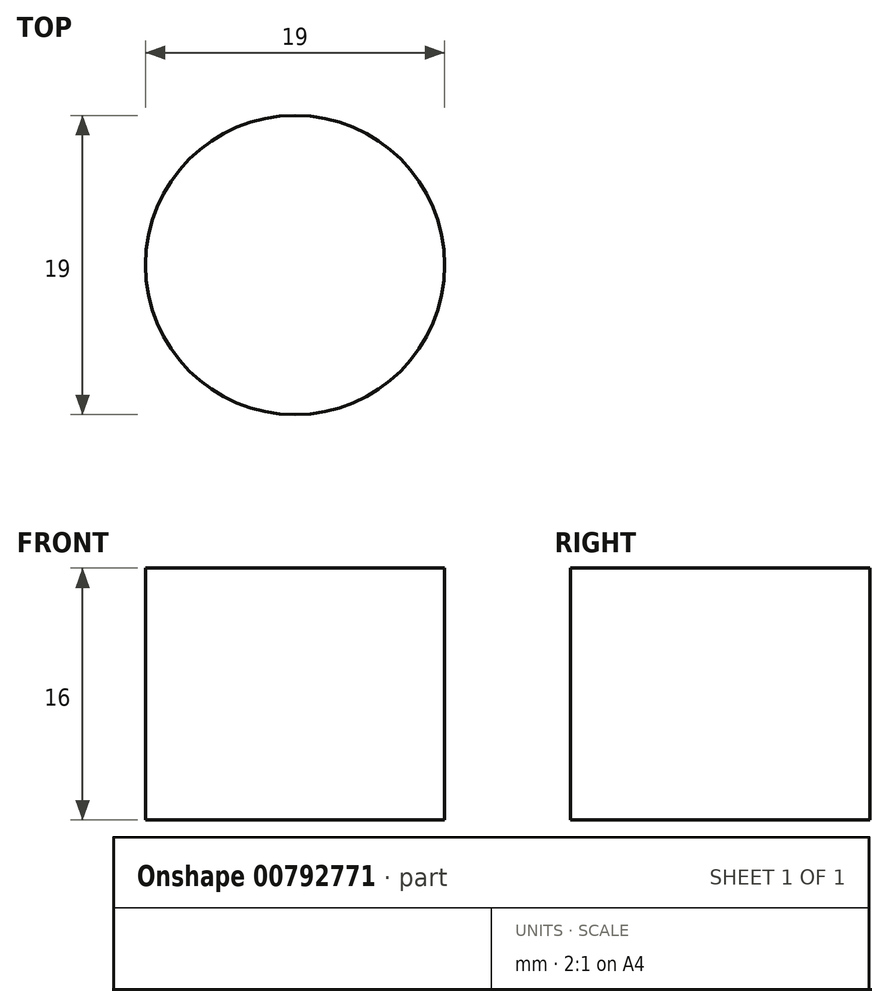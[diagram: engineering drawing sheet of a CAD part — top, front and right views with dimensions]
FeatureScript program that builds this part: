
annotation { "Feature Type Name" : "Feature", "Feature Type Description" : "" }
export const myFeature = defineFeature(function(context is Context, id is Id, definition is map)
    precondition{}
    {
        {
            var Q0;
            Q0=qCreatedBy(makeId("Top.planeOp"),FACE);
            var sketch = newSketch(context, id + "F0", { "sketchPlane" : qUnion([Q0])});
            skCircle(sketch, "E0", {"center": v(0, 0) * mm, "radius": 9.5 * mm});
            skSolve(sketch);
        }
        {
            var Q0;
            Q0=makeQuery(id+"F0.imprint","IMPRINT",FACE,{"disambiguationData":[TD([[makeQuery(id+"F0.imprint","IMPRINT",EDGE,{"derivedFrom":sQuery(id+"F0.wireOp",EDGE,"E0")}),1.0]])]});
            extrude(context, id + "F1", {"entities" : qUnion([Q0]), "depth" : 16 * mm, "offsetDistance" : 25 * mm});
        }
    });
